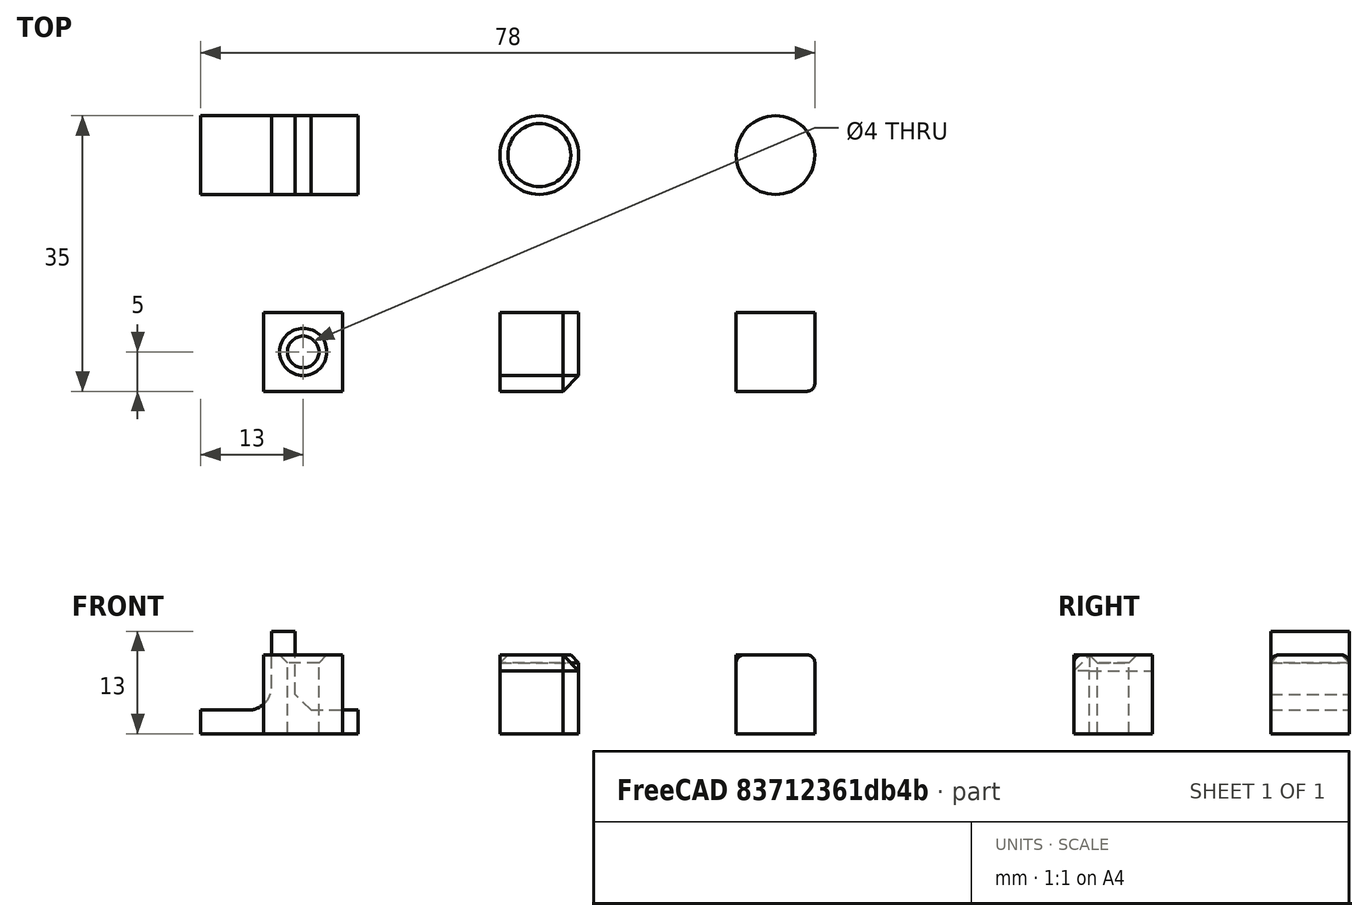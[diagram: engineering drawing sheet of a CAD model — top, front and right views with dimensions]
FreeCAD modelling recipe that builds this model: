
FCSTD DOCUMENT  (FreeCAD 0.18.4R)
Label: tutorial_freecad_ex12_a
License: All rights reserved
LicenseURL: http://en.wikipedia.org/wiki/All_rights_reserved
objects: Part::Box×5, Part::Chamfer×4, Part::Cylinder×3, Part::Fillet×3, Part::Cut×1, Part::MultiFuse×1
note: 17 computed .brp shape members not serialized (recipe doc carries the construction recipe); baked Part::Feature solids carry a one-line shape summary decoded from their .brp

FEATURE [Part::Box] Box  label="Cubo-1"
  AttacherType = Attacher::AttachEngine3D
  Height = 10
  Length = 10
  Placement = pos=(60,0,0) rot=(0,0,1;0rad)
  Width = 10
FEATURE [Part::Box] Box001
  AttacherType = Attacher::AttachEngine3D
  Height = 10
  Length = 10
  Width = 10
FEATURE [Part::Box] Box002  label="Cubo-2"
  AttacherType = Attacher::AttachEngine3D
  Height = 10
  Length = 10
  Placement = pos=(30,0,0) rot=(0,0,1;0rad)
  Width = 10
FEATURE [Part::Cylinder] Cylinder
  Angle = 360
  AttacherType = Attacher::AttachEngine3D
  Height = 20
  Placement = pos=(5,5,-2) rot=(0,0,1;0rad)
  Radius = 2
FEATURE [Part::Cut] Cut  label="Cubo-3"
  Base = -> Box001
  Refine = true
  Tool = -> Cylinder
FEATURE [Part::Cylinder] Cylinder001  label="Cilindro-1"
  Angle = 360
  AttacherType = Attacher::AttachEngine3D
  Height = 10
  Placement = pos=(65,30,0) rot=(0,0,1;0rad)
  Radius = 5
FEATURE [Part::Cylinder] Cylinder002  label="Cilindro-2"
  Angle = 360
  AttacherType = Attacher::AttachEngine3D
  Height = 10
  Placement = pos=(35,30,0) rot=(0,0,1;0rad)
  Radius = 5
FEATURE [Part::Box] Box003
  AttacherType = Attacher::AttachEngine3D
  Height = 3
  Length = 20
  Placement = pos=(-8,25,0) rot=(0,0,1;0rad)
  Width = 10
FEATURE [Part::Box] Box004
  AttacherType = Attacher::AttachEngine3D
  Height = 10
  Length = 3
  Placement = pos=(1,25,3) rot=(0,0,1;0rad)
  Width = 10
FEATURE [Part::MultiFuse] Fusion  label="union-90"
  Refine = true
  Shapes = -> [Box003,Box004]
FEATURE [Part::Fillet] Fillet
  Base = -> Box
  Edges = 3 edges r=1: [Edge5,Edge6,Edge10]
FEATURE [Part::Chamfer] Chamfer
  Base = -> Box002
  Edges = 3 edges r=2: [Edge5,Edge6,Edge10]
FEATURE [Part::Chamfer] Chamfer001
  Base = -> Cut
  Edges = 1 edges r=1: [Edge10]
FEATURE [Part::Fillet] Fillet001
  Base = -> Cylinder001
  Edges = 1 edges r=1: [Edge1]
FEATURE [Part::Chamfer] Chamfer002
  Base = -> Cylinder002
  Edges = 1 edges r=1: [Edge1]
FEATURE [Part::Chamfer] Chamfer003
  Base = -> Fusion
  Edges = 1 edges r=2: [Edge16]
FEATURE [Part::Fillet] Fillet002
  Base = -> Chamfer003
  Edges = 1 edges r=3: [Edge25]
